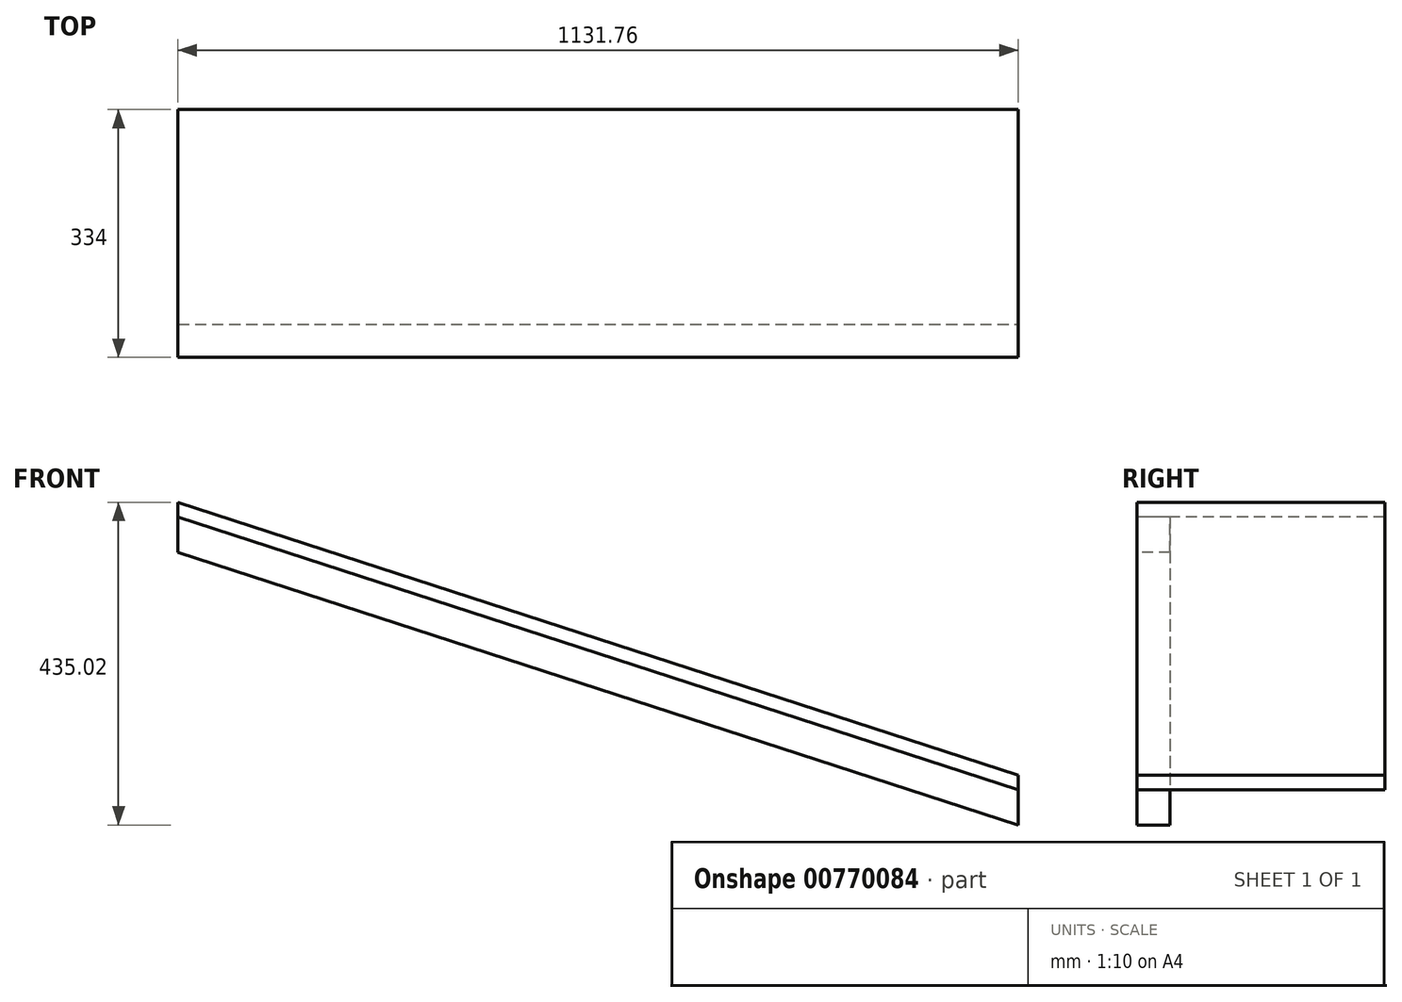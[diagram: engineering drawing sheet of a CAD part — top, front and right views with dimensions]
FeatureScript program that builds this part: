
annotation { "Feature Type Name" : "Feature", "Feature Type Description" : "" }
export const myFeature = defineFeature(function(context is Context, id is Id, definition is map)
    precondition{}
    {
        {
            var Q0;
            Q0=qCreatedBy(makeId("Front.planeOp"),FACE);
            var sketch = newSketch(context, id + "F0", { "sketchPlane" : qUnion([Q0])});
            skLineSegment(sketch, "E0", {"start": v(0, 0) * mm, "end": v(0, 300) * mm});
            skLineSegment(sketch, "E1", {"start": v(0, 300) * mm, "end": v(1131.76, -67.73) * mm});
            skLineSegment(sketch, "E2", {"start": v(0, 300) * mm, "end": v(-5.87, 281.93) * mm});
            skLineSegment(sketch, "E3", {"start": v(-5.87, 281.93) * mm, "end": v(1131.76, -87.7) * mm});
            skLineSegment(sketch, "E4", {"start": v(1131.76, -67.73) * mm, "end": v(1131.76, -87.7) * mm});
            skLineSegment(sketch, "E5", {"start": v(-5.87, 281.93) * mm, "end": v(-5.87, 367.39) * mm});
            skLineSegment(sketch, "E6", {"start": v(-5.87, 281.93) * mm, "end": v(-5.87, 234.61) * mm});
            skLineSegment(sketch, "E7", {"start": v(-5.87, 234.61) * mm, "end": v(1131.76, -135.02) * mm});
            skLineSegment(sketch, "E8", {"start": v(1131.76, -87.7) * mm, "end": v(1131.76, -135.02) * mm});
            skSolve(sketch);
        }
        {
            var Q0;
            {var subQ0=sQuery(id+"F0.wireOp",EDGE,"E1");Q0=makeQuery(id+"F0.imprint","IMPRINT",FACE,{"disambiguationData":[TD([[makeQuery(id+"F0.imprint","IMPRINT",EDGE,{"derivedFrom":subQ0}),-1.0]])]});}
            extrude(context, id + "F1", {"entities" : qUnion([Q0]), "oppositeDirection" : true, "depth" : 334 * mm, "offsetDistance" : 25 * mm});
        }
        {
            var Q0;
            {var subQ5=sQuery(id+"F0.wireOp",EDGE,"E8");Q0=makeQuery(id+"F0.imprint","IMPRINT",FACE,{"disambiguationData":[TD([[makeQuery(id+"F0.imprint","IMPRINT",EDGE,{"derivedFrom":subQ5}),-1.0]])]});}
            extrude(context, id + "F2", {"entities" : qUnion([Q0]), "oppositeDirection" : true, "depth" : 45 * mm, "offsetDistance" : 25 * mm});
        }
    });
